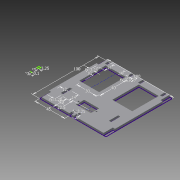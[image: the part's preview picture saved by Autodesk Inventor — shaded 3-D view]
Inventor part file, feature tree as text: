
AUTODESK INVENTOR PART (.ipt)
format: ipt  version: 2013 (Build 170138000, 138)  size: 176,640 bytes
history: native  units: mm
features: extrude x5, other x3, sketch x1
ambient origin geometry x8: Origin, YZ Plane, XZ Plane, XY Plane, X Axis, Y Axis, Z Axis, Center Point
bodies: Solid1 (feature_tree)
feature tree (9):
  other  "Blocks"
  sketch  "Sketch1"  dims[d0=100.0mm d2=100.0mm d3=3.0mm d5=3.0mm d7=3.25mm d8=14.0mm d9=30.0mm d10=40.0mm d11=10.0mm d12=10.0mm d13=3.25mm d14=0.0mm d15=3.25mm d16=8.0mm d17=0.0mm d18=3.25mm d19=0.0mm d20=3.25mm d21=0.0mm d22=22.5mm d23=12.4mm d24=4.5mm d25=4.5mm d26=2.0mm d27=2.0mm d28=22.5mm d29=3.25mm d30=14.0mm d31=12.0mm d32=10.0mm d33=0.0mm d34=20.0mm d35=3.25mm d36=8.0mm d37=45.0mm d38=10.0mm d39=0.0mm]
  extrude  "Extrusion1"  Depth=100.0mm
  extrude  "Extrusion2"  Depth=3.0mm
  extrude  "Extrusion3"  Depth=3.0mm
  extrude  "Extrusion4"  Depth=3.25mm
  extrude  "Extrusion5"  Depth=14.0mm
  other  "Block1"
  other  "Block1:1"
